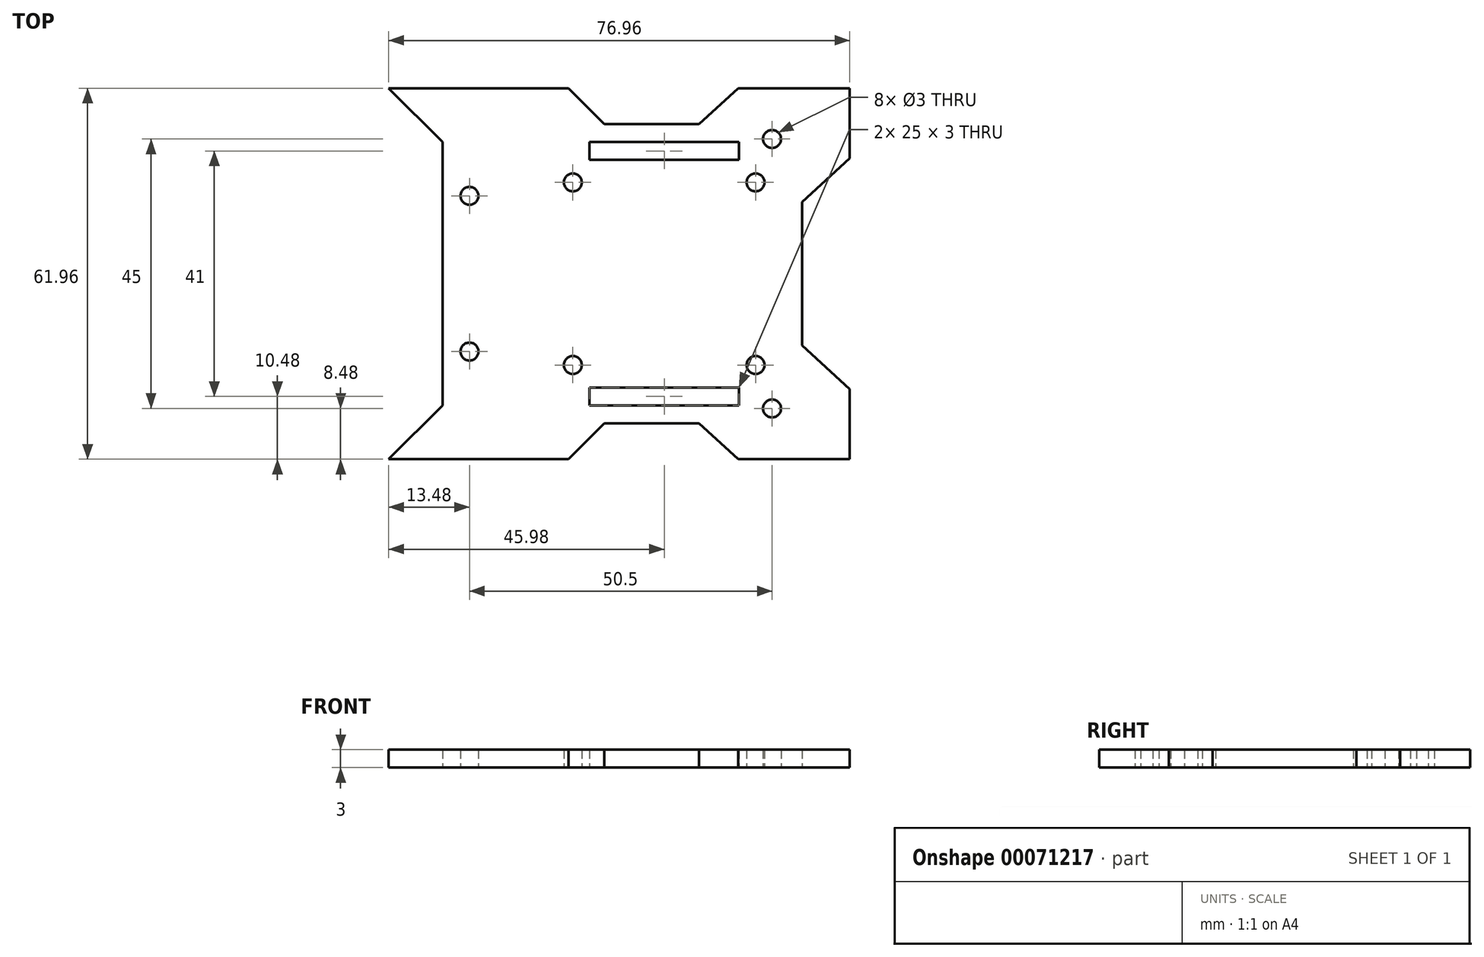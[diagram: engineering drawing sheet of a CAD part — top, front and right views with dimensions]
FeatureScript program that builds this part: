
annotation { "Feature Type Name" : "Feature", "Feature Type Description" : "" }
export const myFeature = defineFeature(function(context is Context, id is Id, definition is map)
    precondition{}
    {
        {
            var Q0;
            Q0=qCreatedBy(makeId("Top.planeOp"),FACE);
            var sketch = newSketch(context, id + "F0", { "sketchPlane" : qUnion([Q0])});
            skPoint(sketch, "E0.rect.middle", {"position": v(0, 0) * mm});
            skLineSegment(sketch, "E1.rect.bottom", {"start": v(18, 18) * mm, "end": v(-18, 18) * mm, "construction": true});
            skLineSegment(sketch, "E1.rect.top", {"start": v(18, -18) * mm, "end": v(-18, -18) * mm, "construction": true});
            skLineSegment(sketch, "E1.rect.left", {"start": v(18, 18) * mm, "end": v(18, -18) * mm, "construction": true});
            skLineSegment(sketch, "E1.rect.right", {"start": v(-18, 18) * mm, "end": v(-18, -18) * mm, "construction": true});
            skLineSegment(sketch, "E2.rect.top", {"start": v(-10, 25) * mm, "end": v(5.83, 25) * mm});
            skLineSegment(sketch, "E2.rect.left", {"start": v(-37, -22) * mm, "end": v(-37, 22) * mm});
            skCircle(sketch, "E3", {"center": v(18, -22.5) * mm, "radius": 1.5 * mm});
            skCircle(sketch, "E4.MirrorC", {"center": v(18, 22.5) * mm, "radius": 1.5 * mm});
            skLineSegment(sketch, "E5", {"start": v(-45.98, -30.98) * mm, "end": v(-37, -22) * mm});
            skLineSegment(sketch, "E6.MirrorCS", {"start": v(-45.98, 30.98) * mm, "end": v(-37, 22) * mm});
            skLineSegment(sketch, "E7.MirrorCS", {"start": v(-15.98, 30.98) * mm, "end": v(-10, 25) * mm});
            skCircle(sketch, "E8", {"center": v(-32.5, -13) * mm, "radius": 1.5 * mm});
            skCircle(sketch, "E9.MirrorC", {"center": v(-32.5, 13) * mm, "radius": 1.5 * mm});
            skLineSegment(sketch, "E10.trimOffspring", {"start": v(23, 12) * mm, "end": v(23, -12) * mm});
            skLineSegment(sketch, "E11.trimOffspring", {"start": v(-10, -25) * mm, "end": v(5.83, -25) * mm});
            skCircle(sketch, "E12", {"center": v(-15.25, 15.25) * mm, "radius": 1.5 * mm});
            skCircle(sketch, "E13.MirrorC", {"center": v(15.25, 15.25) * mm, "radius": 1.5 * mm});
            skCircle(sketch, "E14.MirrorC", {"center": v(-15.25, -15.25) * mm, "radius": 1.5 * mm});
            skCircle(sketch, "E15.MirrorC", {"center": v(15.25, -15.25) * mm, "radius": 1.5 * mm});
            skLineSegment(sketch, "E16.rect.bottom", {"start": v(-12.5, 22) * mm, "end": v(12.5, 22) * mm});
            skLineSegment(sketch, "E16.rect.top", {"start": v(-12.5, 19) * mm, "end": v(12.5, 19) * mm});
            skLineSegment(sketch, "E16.rect.left", {"start": v(-12.5, 22) * mm, "end": v(-12.5, 19) * mm});
            skLineSegment(sketch, "E16.rect.right", {"start": v(12.5, 22) * mm, "end": v(12.5, 19) * mm});
            skPoint(sketch, "E16.rect.middle", {"position": v(0, 20.5) * mm});
            skPoint(sketch, "E17.MirrorP", {"position": v(0, -20.5) * mm});
            skLineSegment(sketch, "E18.MirrorCS", {"start": v(-12.5, -19) * mm, "end": v(12.5, -19) * mm});
            skLineSegment(sketch, "E19.MirrorCS", {"start": v(-12.5, -22) * mm, "end": v(-12.5, -19) * mm});
            skLineSegment(sketch, "E20.MirrorCS", {"start": v(-12.5, -22) * mm, "end": v(12.5, -22) * mm});
            skLineSegment(sketch, "E21.MirrorCS", {"start": v(12.5, -22) * mm, "end": v(12.5, -19) * mm});
            skLineSegment(sketch, "E22", {"start": v(-45.98, 30.98) * mm, "end": v(-15.98, 30.98) * mm});
            skLineSegment(sketch, "E23", {"start": v(12.35, 30.98) * mm, "end": v(30.98, 30.98) * mm});
            skLineSegment(sketch, "E24", {"start": v(30.98, 30.98) * mm, "end": v(30.98, 19.3) * mm});
            skLineSegment(sketch, "E25", {"start": v(30.98, -30.98) * mm, "end": v(12.35, -30.98) * mm});
            skLineSegment(sketch, "E26.trimOffspring", {"start": v(30.98, -19.3) * mm, "end": v(30.98, -30.98) * mm});
            skLineSegment(sketch, "E27.trimOffspring", {"start": v(-15.98, -30.98) * mm, "end": v(-45.98, -30.98) * mm});
            skLineSegment(sketch, "E28", {"start": v(5.83, 25) * mm, "end": v(12.35, 30.98) * mm});
            skLineSegment(sketch, "E29", {"start": v(23, 12) * mm, "end": v(30.98, 19.3) * mm});
            skLineSegment(sketch, "E30", {"start": v(23, -12) * mm, "end": v(30.98, -19.3) * mm});
            skLineSegment(sketch, "E31", {"start": v(12.35, -30.98) * mm, "end": v(5.83, -25) * mm});
            skLineSegment(sketch, "E32", {"start": v(-10, -25) * mm, "end": v(-15.98, -30.98) * mm});
            skSolve(sketch);
        }
        {
            var Q0;
            Q0 = qSketchRegion(id + "F0", true);
            extrude(context, id + "F1", {"entities" : qUnion([Q0]), "depth" : 3 * mm});
        }
    });
